# Revit family: Sink-Double Bowl-Clark Monaco Scalloped Undermount1
name_source: partatom
category: Plumbing Fixtures
revit_build: Autodesk Revit Architecture 2012 (Build: 20110916_2132(x64)
units: mm (PartAtom-declared; Revit-internal decimal feet)

## types (1)
- Monaco
    Assembly Code = D2010410
    CW Connection = No
    Cost = 0 $
    Default Elevation = 0 mm  [stored 0 ft]
    Depth_ANZRS = 190 mm
    Description = Monaco Scalloped Double Bowl Undermount
    HW Connection = No
    Keynote = SK
    Length_ANZRS = 750 mm  [stored 2.46063 ft]
    Manufacturer = Clark
    Material_ANZRS = Metal-Stainless-Caroma
    Model = 5908
    Type Comments = Includes bamboo board, SS colander, SS draining tray and basket wastes, Bowl Volume 23L per bowl, Carton size 900 x 565 x 240, Carton weight 8.35kg, Match with Caroma Liano mixer range
    URL = http://www.clark.com.au
    Vent Connection = No
    WFU = 2
    Waste Connection = Yes
    Waste Radius = 25 mm  [stored 0.082021 ft]
    Width_ANZRS = 470 mm  [stored 1.54199 ft]

note: [stored X ft] marks values corroborated as IEEE doubles in the binary element streams (Revit-internal decimal feet)

## geometry (parser evidence)
native form markers: Blend x4, Sweep x2
no freeform markers — native parametric forms only
